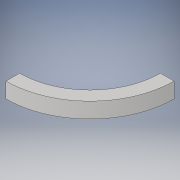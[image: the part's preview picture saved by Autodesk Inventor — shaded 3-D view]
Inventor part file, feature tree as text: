
AUTODESK INVENTOR PART (.ipt)
format: ipt  version: 2017 (Build 210142000, 142)  size: 134,656 bytes
history: native  units: in
note: dims shown in document units (in); Inventor stores cm internally (conversion verified against a paired STEP export)
features: revolve x1, sketch x1
ambient origin geometry x8: Origin, YZ Plane, XZ Plane, XY Plane, X Axis, Y Axis, Z Axis, Center Point
bodies: Solid1 (feature_tree)
feature tree (2):
  revolve  "Revolution1"  [1 undecoded]
  sketch  "Sketch1"  dims[d1=0.9911in d2=5.1195in d3=1.7489in d4=0.0in d5=0.0625in d6=0.0625in d7=0.0625in d8=0.0625in d9=0.7182in d10=0.3125in d11=0.1562in d12=90.0deg d13=0.8745in d14=0.0312in d15=0.25in d16=0.25in]
note: 1 required parameter value undecoded (feature->parameter linkage not recoverable at this tier; creation-order binding heuristic only, values carry confidence <= 0.55)
